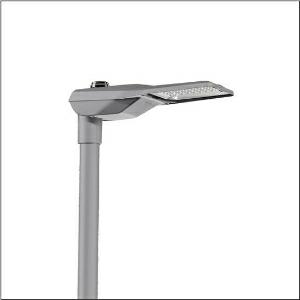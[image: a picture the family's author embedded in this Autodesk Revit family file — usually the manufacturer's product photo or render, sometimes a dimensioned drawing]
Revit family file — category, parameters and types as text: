
# Revit family: streetlight_sl_21_mini___stw1_0a_5xe6e47n08jb_ac66
name_source: partatom
category: Lighting Fixtures
units: mm (PartAtom-declared; Revit-internal decimal feet)

## family parameters
Cut with Voids When Loaded = No
Host = Face
Light Source = No
Part Type = Normal
Room Calculation Point = No
Round Connector Dimension = Use Diameter
Shared = No

## types (1)
- --- (1 x LED, 13390 lm, 87.3 W, 4000K)
    Apparent Load = 87 VA
    CIE Flux Codes = 39 75 98 100 100
    Color Rendering = 70
    Color Temperature = 4000K
    Default Elevation = 1800 mm
    Description = Streetlight SL 21 mini, mast luminaire, primary light control with lens, of PMMA, primary optical cover: cover, of toughened safety glass, transparent, light distribution: STW1.0a, light emission: direct distribution, primary light characteristic: asymmetric, installation type: side-entry, LED, 3G 2.5mm², High Power LED, rated luminous flux: 13.390lm, luminous efficacy: 153lm/W, light colour: 740, colour temperature: 4000K, control gear: NEMA (7pin), control: overheat protection, pre-setting: linear dimming characteristic, constant luminous flux control, time-dependent luminous flux control, flexible luminous flux parameterisation, mains connection: 230..240V, AC, 50/60Hz, connection cable pre-assembled, cable length: 10,5m, wiring characteristics: H05VV-F, start of lifetime: 87W, end of service life: 90W, reduction: 40W, luminaire housing, of diecast aluminium (EN AC-44300), powder-coated, Siteco® metallic grey (DB 702S), corrosivity category C5 mid according to DIN EN ISO 12944, multi-level sealing system, sealing non-destructively replaceable, inclination adjustable: 0°, 5°, 10°, 15°, length: 628mm, width: 235mm, height: 110mm, spigot size: 42mm (side-entry), mounting height: 4..8m, protection rating (complete): IP66, insulation class (complete): insulation class I (protective earthing), certification: CE, ENEC, ENEC+, VDE, impact resistance: IK10, permissible operating ambient temperature for outdoor applications: -40..+50°C, standard-compliant lighting for roads and squares, packaging unit: 1 piece

Light Distribution: STW1.0a
    Height = 110 mm
    Lamp = 1 x LED
    Lamp Light Flux = 13390 lm
    Lamp Power = 87.3 W
    Lamp count = 1
    Length = 625 mm
    Luminous efficacy = 153 lm/W
    Manufacturer = Siteco
    ModVariant = No
    Model = 5XE6E47N08JB
    Number of Poles = 1
    OnlyDefault = Yes
    Power Factor = 1
    Product Name = Streetlight SL 21 mini | STW1.0a
    Product group = mast luminaire | pylon top
    ProductGroupID = 6100
    Protection Class = Protection class I
    Protection Degree = IP 66
    RLX_Detail_Level = 1
    RLX_Emergency_Light_Flux = 0 lm
    RLX_Emergency_Type = 0
    RLX_Emergency_Type_DB = No
    RlxData = <blob elided: 26081 chars, md5=ac3174d5>
    Socket = socket
    Standby Power = 0 W
    System Light Flux = 13390 lm
    System Power = 87 W
    Type Comments = factory setting: luminous flux: 100 % | dim-lin: 254 | 915 mA
    Type Image = l_1294379.jpg
    URL = http://relux.com
    VarID = @adj_156451
    Voltage = 0 V
    Weight = 0.00 kg
    Width = 234 mm

## geometry (parser evidence)
native form markers: Blend x4, Sweep x13
no freeform markers — native parametric forms only
